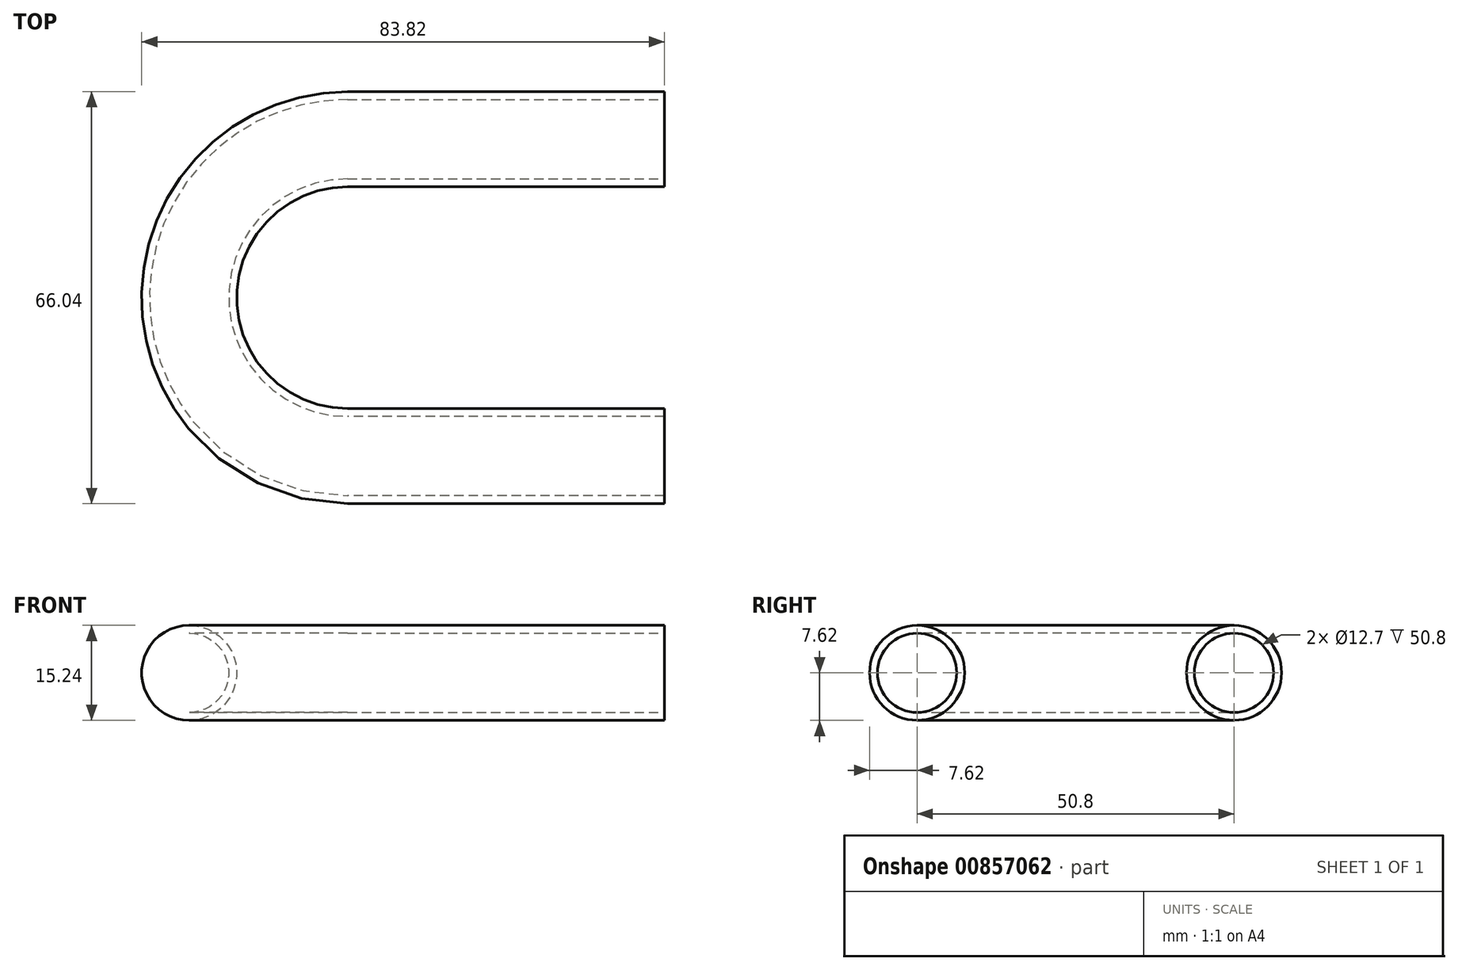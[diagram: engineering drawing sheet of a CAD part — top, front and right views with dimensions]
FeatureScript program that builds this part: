
annotation { "Feature Type Name" : "Feature", "Feature Type Description" : "" }
export const myFeature = defineFeature(function(context is Context, id is Id, definition is map)
    precondition{}
    {
        {
            var Q0;
            Q0=qCreatedBy(makeId("Top.planeOp"),FACE);
            var sketch = newSketch(context, id + "F0", { "sketchPlane" : qUnion([Q0])});
            skLineSegment(sketch, "E0", {"start": v(0, 0) * mm, "end": v(-50.8, 0) * mm});
            skLineSegment(sketch, "E1", {"start": v(-50.8, 50.8) * mm, "end": v(0, 50.8) * mm});
            skLineSegment(sketch, "E2", {"start": v(-50.8, 50.8) * mm, "end": v(-50.8, 0) * mm});
            skLineSegment(sketch, "E3", {"start": v(-50.8, 0) * mm, "end": v(-50.8, -50.8) * mm});
            skArc(sketch, "E4", {"start": v(-50.8, 50.8) * mm, "mid": v(-76.2, 25.4) * mm, "end": v(-50.8, 0) * mm});
            skSolve(sketch);
        }
        {
            var Q0;
            Q0=qCreatedBy(makeId("Right.planeOp"),FACE);
            var sketch = newSketch(context, id + "F1", { "sketchPlane" : qUnion([Q0])});
            skCircle(sketch, "E5", {"center": v(0, 0) * mm, "radius": 6.35 * mm});
            skCircle(sketch, "E6", {"center": v(0, 0) * mm, "radius": 7.62 * mm});
            skSolve(sketch);
        }
        {
            var Q0;
            Q0=makeQuery(id+"F1.imprint","IMPRINT",FACE,{"disambiguationData":[TD([[makeQuery(id+"F1.imprint","IMPRINT",EDGE,{"derivedFrom":sQuery(id+"F1.wireOp",EDGE,"E5")}),-1.0]])]});
            var Q1;
            Q1=sQuery(id+"F0.wireOp",EDGE,"E0");
            var Q2;
            Q2=sQuery(id+"F0.wireOp",EDGE,"E1");
            var Q3;
            Q3=sQuery(id+"F0.wireOp",EDGE,"E4");
            sweep(context, id + "F2", {"profiles" : qUnion([Q0]), "path" : qUnion([Q1, Q2, Q3])});
        }
    });
